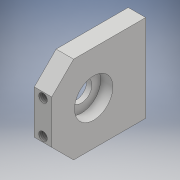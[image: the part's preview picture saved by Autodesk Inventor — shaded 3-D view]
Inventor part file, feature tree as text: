
AUTODESK INVENTOR PART (.ipt)
format: ipt  version: 2018 (Build 220112000, 112)  size: 145,920 bytes
history: native  units: mm
features: sketch x5, extrude x3, hole x2
ambient origin geometry x8: Origin, YZ Plane, XZ Plane, XY Plane, X Axis, Y Axis, Z Axis, Center Point
bodies: Solid1 (feature_tree)
feature tree (10):
  extrude  "Extrusion1"  Depth=12.5mm
  extrude  "Extrusion2"  Depth=53.8mm
  extrude  "Extrusion3"  TaperAngle=0.0deg  [1 undecoded]
  hole  "Hole1"  [1 undecoded]
  hole  "Hole2"  [1 undecoded]
  sketch  "Sketch1"  dims[d1=50.0mm d2=12.5mm]
  sketch  "Sketch2"  dims[d3=45.0deg d4=53.8mm]
  sketch  "Sketch3"  dims[d5=10.0mm d6=0.0mm]
  sketch  "Sketch4"  dims[d7=22.0mm d8=29.8mm]
  sketch  "Sketch5"  dims[d9=25.0mm d10=7.0mm d11=0.0mm d12=12.0mm d13=7.0mm d14=0.0mm d15=10.0mm d16=5.0mm d17=4.917mm d18=12.0mm d19=4.0mm d20=2.0mm d21=90.0deg d22=28.0mm d23=20.594885mm d24=5.0mm d25=3.0mm d26=4.917mm d27=12.0mm d28=4.0mm d29=2.0mm d30=90.0deg d31=13.0mm d32=20.594885mm]
note: 3 required parameter values undecoded (feature->parameter linkage not recoverable at this tier; creation-order binding heuristic only, values carry confidence <= 0.55)
